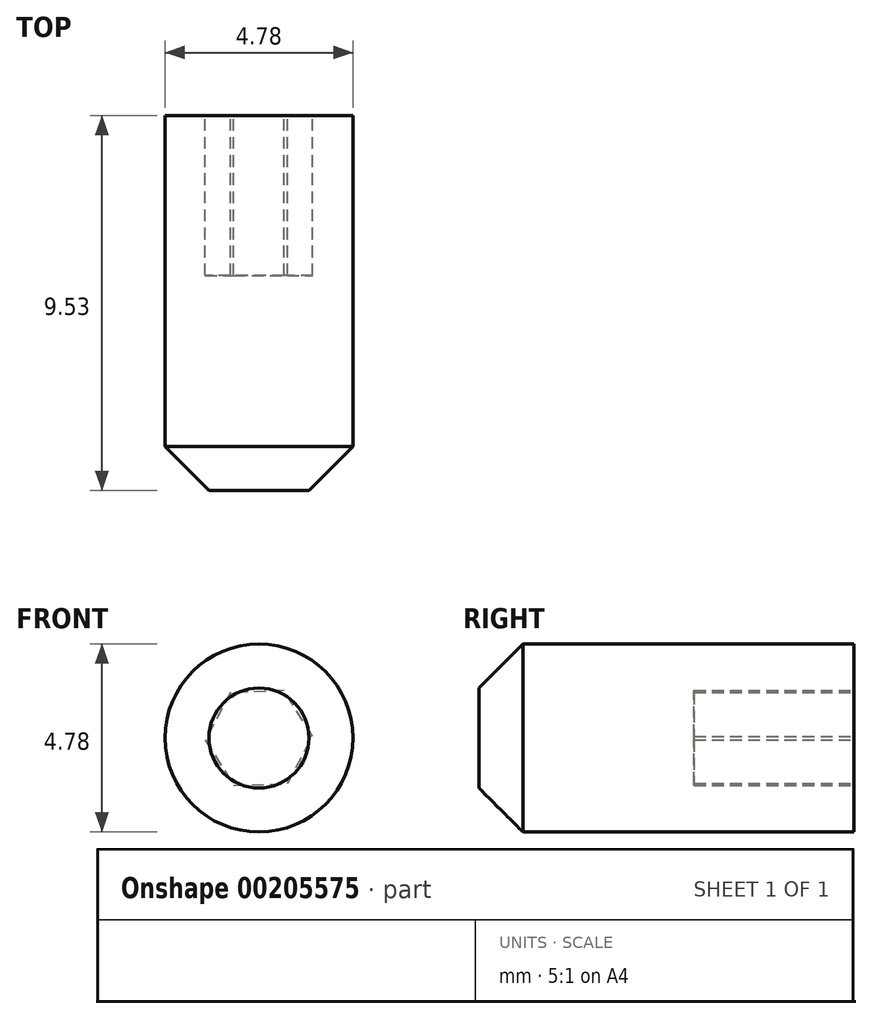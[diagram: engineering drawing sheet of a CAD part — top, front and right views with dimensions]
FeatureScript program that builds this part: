
annotation { "Feature Type Name" : "Feature", "Feature Type Description" : "" }
export const myFeature = defineFeature(function(context is Context, id is Id, definition is map)
    precondition{}
    {
        {
            var Q0;
            Q0=qCreatedBy(makeId("Front.planeOp"),FACE);
            var sketch = newSketch(context, id + "F0", { "sketchPlane" : qUnion([Q0])});
            skCircle(sketch, "E0", {"center": v(0, 0) * mm, "radius": 2.39 * mm});
            skSolve(sketch);
        }
        {
            var Q0;
            Q0=qSketchRegion(id+"F0",true);
            extrude(context, id + "F1", {"entities" : qUnion([Q0]), "oppositeDirection" : true, "depth" : 9.52 * mm});
        }
        {
            var Q0;
            Q0=makeQuery(id+"F1.opExtrude","CAP_FACE",FACE,{"disambiguationData":[OSD([sQuery(id+"F0.wireOp",EDGE,"E0")])],"isStart":false});
            var sketch = newSketch(context, id + "F2", { "sketchPlane" : qUnion([Q0])});
            skCircle(sketch, "E1.cCircle", {"center": v(0, 0) * mm, "radius": 1.18 * mm, "construction": true});
            skLineSegment(sketch, "E1.0", {"start": v(-0.72, -1.16) * mm, "end": v(-1.36, 0.05) * mm});
            skLineSegment(sketch, "E1.1", {"start": v(-1.36, 0.05) * mm, "end": v(-0.64, 1.2) * mm});
            skLineSegment(sketch, "E1.2", {"start": v(-0.64, 1.2) * mm, "end": v(0.72, 1.16) * mm});
            skLineSegment(sketch, "E1.3", {"start": v(0.72, 1.16) * mm, "end": v(1.36, -0.05) * mm});
            skLineSegment(sketch, "E1.4", {"start": v(1.36, -0.05) * mm, "end": v(0.64, -1.2) * mm});
            skLineSegment(sketch, "E1.5", {"start": v(0.64, -1.2) * mm, "end": v(-0.72, -1.16) * mm});
            skPoint(sketch, "E1.0.midPoint", {"position": v(-1.04, -0.55) * mm});
            skSolve(sketch);
        }
        {
            var Q0;
            Q0=qSketchRegion(id+"F2",true);
            extrude(context, id + "F3", {"entities" : qUnion([Q0]), "operationType" : NewBodyOperationType.REMOVE, "oppositeDirection" : true, "depth" : 4.06 * mm});
        }
        {
            var Q0;
            Q0=makeQuery(id+"F1.opExtrude","CAP_EDGE",EDGE,{"disambiguationData":[OSD([sQuery(id+"F0.wireOp",EDGE,"E0")])],"isStart":true});
            chamfer(context, id + "F4", {"entities" : qUnion([Q0]), "width" : 1.12 * mm, "tangentPropagation" : true});
        }
    });
